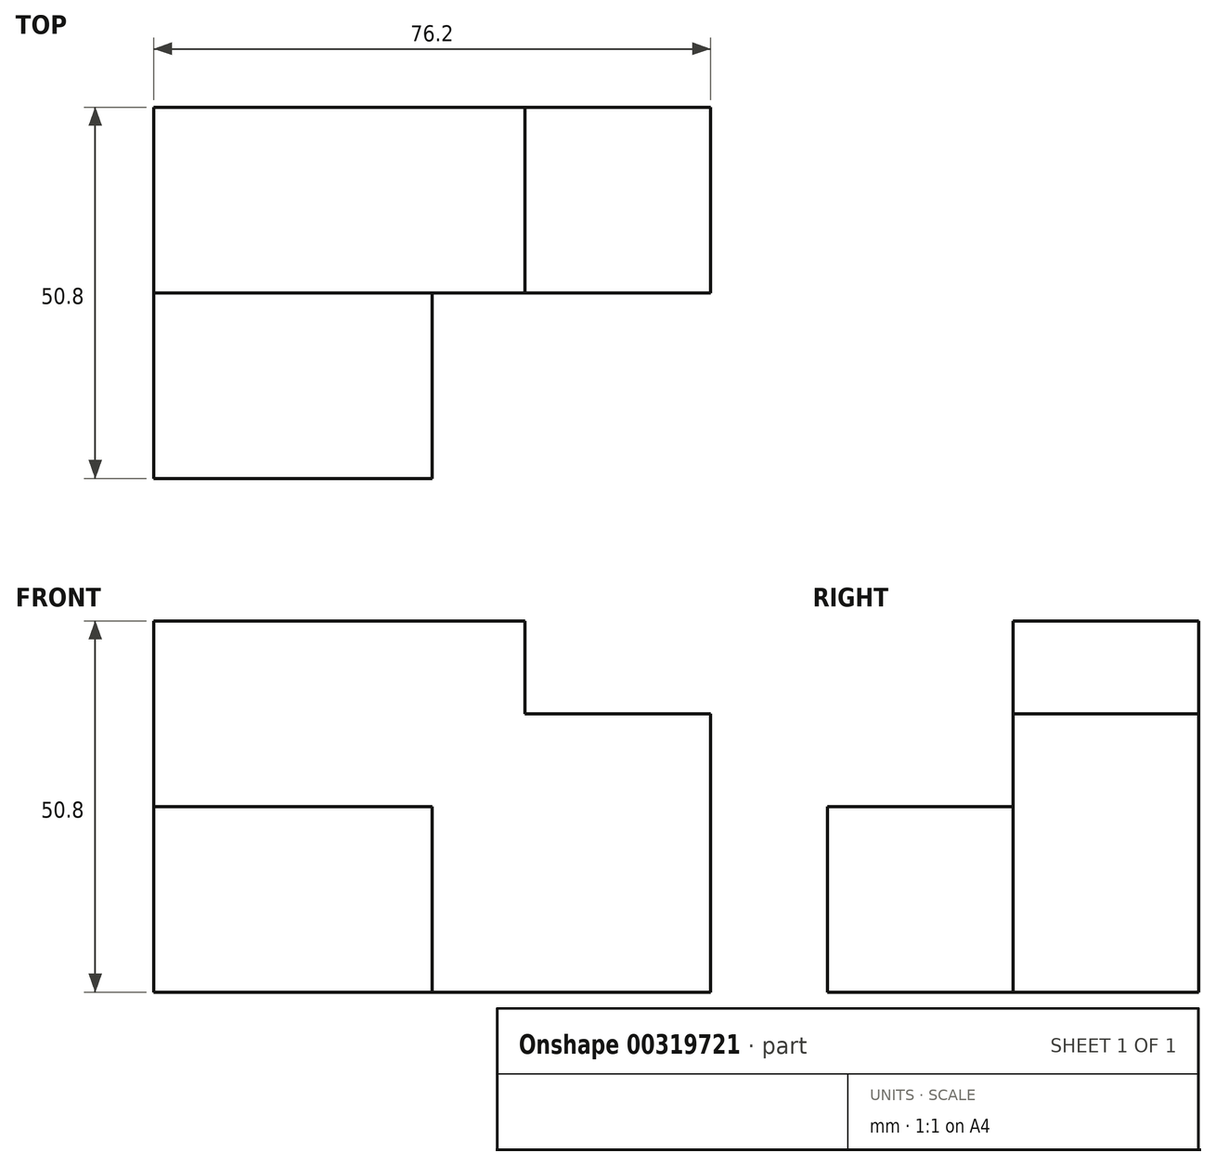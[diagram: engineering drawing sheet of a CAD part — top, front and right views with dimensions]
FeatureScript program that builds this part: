
annotation { "Feature Type Name" : "Feature", "Feature Type Description" : "" }
export const myFeature = defineFeature(function(context is Context, id is Id, definition is map)
    precondition{}
    {
        {
            var Q0;
            Q0=qCreatedBy(makeId("Front.planeOp"),FACE);
            var sketch = newSketch(context, id + "F0", { "sketchPlane" : qUnion([Q0])});
            skLineSegment(sketch, "E0", {"start": v(-36.69, 20) * mm, "end": v(39.51, 20) * mm});
            skLineSegment(sketch, "E1", {"start": v(39.51, 20) * mm, "end": v(39.51, -18.1) * mm});
            skLineSegment(sketch, "E2", {"start": v(39.51, -18.1) * mm, "end": v(-36.69, -18.1) * mm});
            skLineSegment(sketch, "E3", {"start": v(-36.69, -18.1) * mm, "end": v(-36.69, 20) * mm});
            skSolve(sketch);
        }
        {
            var Q0;
            Q0=makeQuery(id+"F0.imprint","IMPRINT",FACE,{"disambiguationData":[TD([[makeQuery(id+"F0.imprint","IMPRINT",EDGE,{"derivedFrom":sQuery(id+"F0.wireOp",EDGE,"E0")}),-1.0]])]});
            extrude(context, id + "F1", {"entities" : qUnion([Q0]), "depth" : 25.4 * mm});
        }
        {
            var Q0;
            Q0=makeQuery(id+"F1.opExtrude","CAP_FACE",FACE,{"disambiguationData":[OSD([sQuery(id+"F0.wireOp",EDGE,"E0"),sQuery(id+"F0.wireOp",EDGE,"E1"),sQuery(id+"F0.wireOp",EDGE,"E2"),sQuery(id+"F0.wireOp",EDGE,"E3")])],"isStart":false});
            var sketch = newSketch(context, id + "F2", { "sketchPlane" : qUnion([Q0])});
            skLineSegment(sketch, "E4", {"start": v(-36.69, -18.1) * mm, "end": v(1.41, -18.1) * mm});
            skLineSegment(sketch, "E5", {"start": v(1.41, -18.1) * mm, "end": v(1.41, 7.3) * mm});
            skLineSegment(sketch, "E6", {"start": v(1.41, 7.3) * mm, "end": v(-36.69, 7.3) * mm});
            skSolve(sketch);
        }
        {
            var Q0;
            {var subQ0=sQuery(id+"F2.wireOp",EDGE,"E4");Q0=makeQuery(id+"F2.imprint","IMPRINT",FACE,{"disambiguationData":[TD([[makeQuery(id+"F2.imprint","IMPRINT",EDGE,{"derivedFrom":subQ0}),-1.0]])]});}
            extrude(context, id + "F3", {"entities" : qUnion([Q0]), "operationType" : NewBodyOperationType.ADD, "depth" : 25.4 * mm});
        }
        {
            var Q0;
            Q0=makeQuery(id+"F1.opExtrude","SWEPT_FACE",FACE,{"disambiguationData":[OSD([sQuery(id+"F0.wireOp",EDGE,"E0")])]});
            var sketch = newSketch(context, id + "F4", { "sketchPlane" : qUnion([Q0])});
            skLineSegment(sketch, "E7", {"start": v(14.11, -25.4) * mm, "end": v(14.11, 0) * mm});
            skLineSegment(sketch, "E8", {"start": v(14.11, 0) * mm, "end": v(-36.69, 0) * mm});
            skLineSegment(sketch, "E9", {"start": v(-36.69, 0) * mm, "end": v(-36.69, -25.4) * mm});
            skLineSegment(sketch, "E10", {"start": v(-36.69, -25.4) * mm, "end": v(14.11, -25.4) * mm});
            skSolve(sketch);
        }
        {
            var Q0;
            Q0=makeQuery(id+"F4.imprint","IMPRINT",FACE,{"disambiguationData":[TD([[makeQuery(id+"F4.imprint","IMPRINT",EDGE,{"derivedFrom":sQuery(id+"F4.wireOp",EDGE,"E7")}),1.0]])]});
            extrude(context, id + "F5", {"entities" : qUnion([Q0]), "operationType" : NewBodyOperationType.ADD, "depth" : 12.7 * mm});
        }
    });
